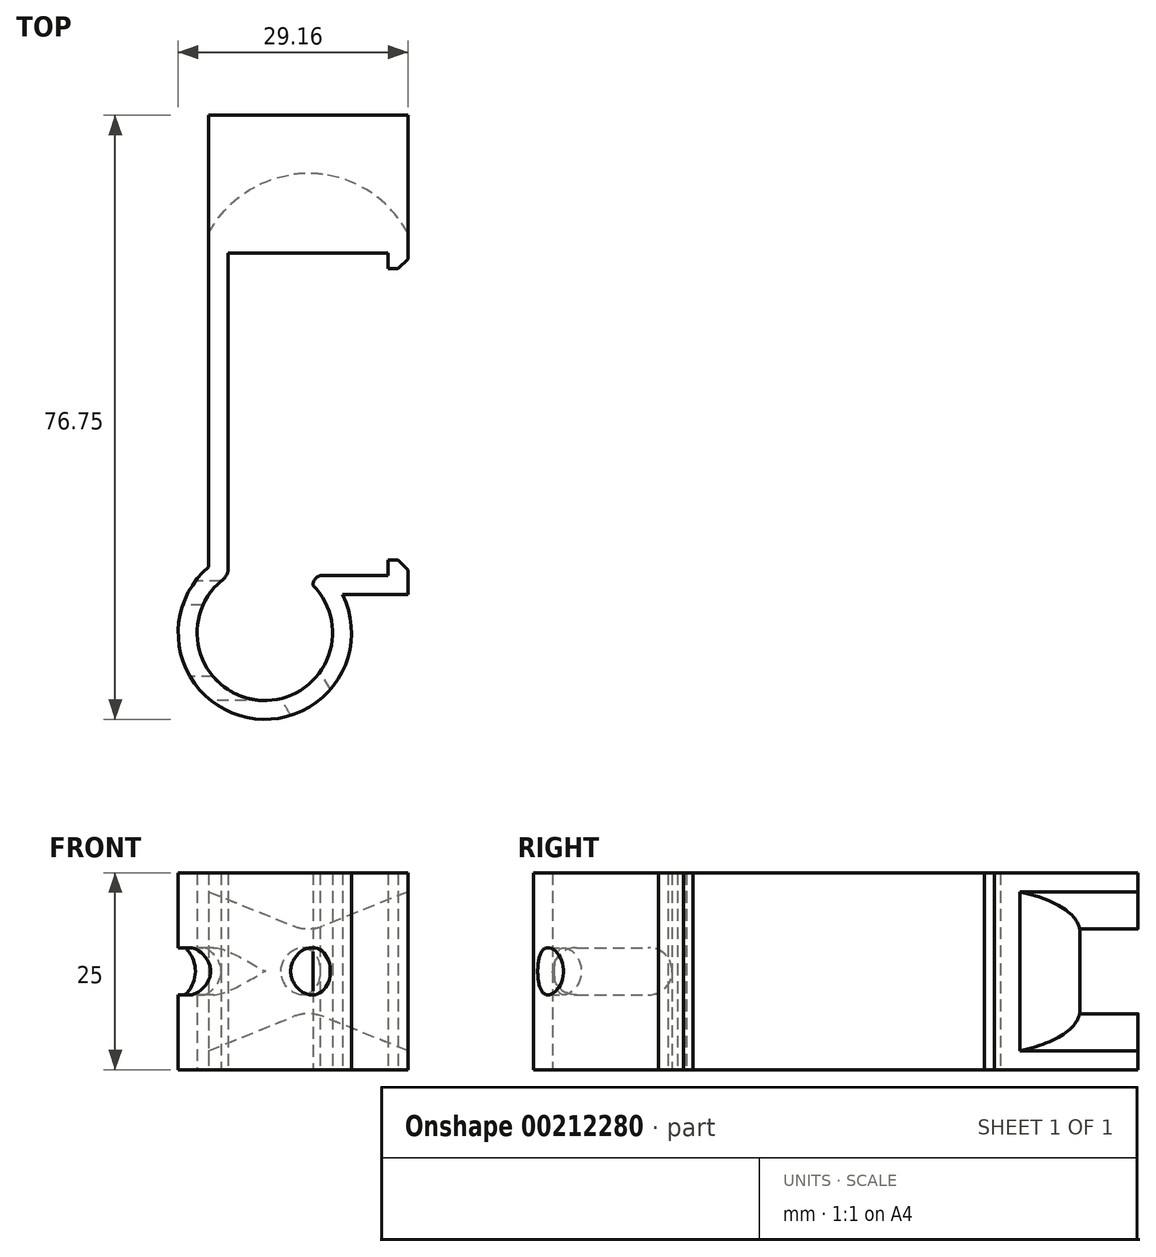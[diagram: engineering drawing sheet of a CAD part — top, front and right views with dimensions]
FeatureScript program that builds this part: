
annotation { "Feature Type Name" : "Feature", "Feature Type Description" : "" }
export const myFeature = defineFeature(function(context is Context, id is Id, definition is map)
    precondition{}
    {
        {
            var Q0;
            Q0=qCreatedBy(makeId("Top.planeOp"),FACE);
            var sketch = newSketch(context, id + "F0", { "sketchPlane" : qUnion([Q0])});
            skLineSegment(sketch, "E0", {"start": v(0, 0) * mm, "end": v(20.3, 0) * mm});
            skLineSegment(sketch, "E1", {"start": v(20.3, 0) * mm, "end": v(20.3, -2) * mm});
            skLineSegment(sketch, "E2", {"start": v(20.3, -2) * mm, "end": v(21.55, -2) * mm});
            skLineSegment(sketch, "E3", {"start": v(22.8, -0.75) * mm, "end": v(22.8, 2.5) * mm});
            skLineSegment(sketch, "E4", {"start": v(22.8, 2.5) * mm, "end": v(-2.5, 2.5) * mm});
            skLineSegment(sketch, "E5", {"start": v(-2.5, 2.5) * mm, "end": v(-2.5, -39.87) * mm});
            skLineSegment(sketch, "E6", {"start": v(0, 0) * mm, "end": v(0, -40.08) * mm});
            skLineSegment(sketch, "E7", {"start": v(21.55, -2) * mm, "end": v(22.8, -0.75) * mm});
            skPoint(sketch, "E8.orphan", {"position": v(22.8, -2) * mm});
            skLineSegment(sketch, "E9", {"start": v(0, -20.5) * mm, "end": v(14.17, -20.5) * mm});
            skPoint(sketch, "E9.endSnap0", {"position": v(0, -20.5) * mm});
            skPoint(sketch, "E10.MirrorP", {"position": v(22.8, -39) * mm});
            skLineSegment(sketch, "E11.MirrorCS", {"start": v(20.3, -41) * mm, "end": v(20.3, -39) * mm});
            skLineSegment(sketch, "E12.MirrorCS", {"start": v(20.3, -39) * mm, "end": v(21.55, -39) * mm});
            skLineSegment(sketch, "E13.MirrorCS", {"start": v(21.55, -39) * mm, "end": v(22.8, -40.25) * mm});
            skLineSegment(sketch, "E14.MirrorCS", {"start": v(22.8, -40.25) * mm, "end": v(22.8, -43.4) * mm});
            skLineSegment(sketch, "E15", {"start": v(20.3, -41) * mm, "end": v(11.67, -41) * mm});
            skLineSegment(sketch, "E16", {"start": v(22.8, -43.4) * mm, "end": v(14.52, -43.4) * mm});
            skPoint(sketch, "E17.orphan", {"position": v(9.28, -43.4) * mm});
            skArc(sketch, "E18", {"start": v(-0.56, -41.4) * mm, "mid": v(4.02, -56.83) * mm, "end": v(10.78, -42.21) * mm});
            skArc(sketch, "E19.0", {"start": v(-2.5, -39.87) * mm, "mid": v(2.4, -59.02) * mm, "end": v(14.52, -43.4) * mm});
            skArc(sketch, "E20", {"start": v(11.67, -41) * mm, "mid": v(11, -41.44) * mm, "end": v(10.78, -42.21) * mm});
            skPoint(sketch, "E21.orphan", {"position": v(9.28, -41) * mm});
            skPoint(sketch, "E22.orphan", {"position": v(-2.5, -41) * mm});
            skArc(sketch, "E23", {"start": v(-0.9, -41.67) * mm, "mid": v(-0.25, -40.99) * mm, "end": v(0, -40.08) * mm});
            skPoint(sketch, "E24.orphan", {"position": v(0, -41) * mm});
            skSolve(sketch);
        }
        {
            var Q0;
            Q0 = qSketchRegion(id + "F0", true);
            extrude(context, id + "F1", {"entities" : qUnion([Q0]), "depth" : 25 * mm});
        }
        {
            var Q0;
            Q0=makeQuery(id+"F1.opExtrude","CAP_FACE",FACE,{"disambiguationData":[OSD([sQuery(id+"F0.wireOp",EDGE,"E0"),sQuery(id+"F0.wireOp",EDGE,"E1"),sQuery(id+"F0.wireOp",EDGE,"E2"),sQuery(id+"F0.wireOp",EDGE,"E3"),sQuery(id+"F0.wireOp",EDGE,"E4"),sQuery(id+"F0.wireOp",EDGE,"E5"),sQuery(id+"F0.wireOp",EDGE,"E6"),sQuery(id+"F0.wireOp",EDGE,"E7"),sQuery(id+"F0.wireOp",EDGE,"E11.MirrorCS"),sQuery(id+"F0.wireOp",EDGE,"E12.MirrorCS"),sQuery(id+"F0.wireOp",EDGE,"E13.MirrorCS"),sQuery(id+"F0.wireOp",EDGE,"E14.MirrorCS"),sQuery(id+"F0.wireOp",EDGE,"E15"),sQuery(id+"F0.wireOp",EDGE,"E16"),sQuery(id+"F0.wireOp",EDGE,"E18"),sQuery(id+"F0.wireOp",EDGE,"E19.0"),sQuery(id+"F0.wireOp",EDGE,"E20"),sQuery(id+"F0.wireOp",EDGE,"E23")])],"isStart":false});
            var sketch = newSketch(context, id + "F2", { "sketchPlane" : qUnion([Q0])});
            skLineSegment(sketch, "E25", {"start": v(4.24, -56.84) * mm, "end": v(-14.11, -38.5) * mm});
            skLineSegment(sketch, "E26", {"start": v(4.24, -56.84) * mm, "end": v(28.92, -42.6) * mm});
            skLineSegment(sketch, "E27", {"start": v(-16.07, -56.84) * mm, "end": v(26.6, -56.84) * mm});
            skSolve(sketch);
        }
        {
            var Q0;
            Q0=sQuery(id+"F2.wireOp",EDGE,"E26");
            cPlane(context, id + "F3", {"entities" : qUnion([Q0]), "cplaneType" : CPlaneType.LINE_ANGLE, "offset" : 25 * mm, "angle" : 0 * degree, "width" : 150 * mm, "height" : 150 * mm});
        }
        {
            var Q0;
            Q0=qCreatedBy(id+"F3.planeOp",FACE);
            var sketch = newSketch(context, id + "F4", { "sketchPlane" : qUnion([Q0])});
            skLineSegment(sketch, "E28.0", {"start": v(11.5, 25) * mm, "end": v(28.71, 25) * mm});
            skLineSegment(sketch, "E28.1", {"start": v(11.5, 0) * mm, "end": v(28.71, 0) * mm});
            skLineSegment(sketch, "E29", {"start": v(11.5, 25) * mm, "end": v(11.5, 0) * mm});
            skLineSegment(sketch, "E30", {"start": v(11.5, 12.5) * mm, "end": v(28.71, 12.5) * mm});
            skCircle(sketch, "E31", {"center": v(19.5, 12.5) * mm, "radius": 3 * mm});
            skSolve(sketch);
        }
        {
            var Q0;
            Q0 = qSketchRegion(id + "F4", true);
            extrude(context, id + "F5", {"entities" : qUnion([Q0]), "operationType" : NewBodyOperationType.REMOVE, "oppositeDirection" : true, "depth" : 7.7 * mm});
        }
        {
            var Q0;
            Q0=makeQuery(id+"F1.opExtrude","SWEPT_FACE",FACE,{"disambiguationData":[OSD([sQuery(id+"F0.wireOp",EDGE,"E5")])]});
            var sketch = newSketch(context, id + "F6", { "sketchPlane" : qUnion([Q0])});
            skLineSegment(sketch, "E32.0", {"start": v(41.67, 0) * mm, "end": v(56.85, 0) * mm});
            skLineSegment(sketch, "E33.0", {"start": v(41.67, 25) * mm, "end": v(56.85, 25) * mm});
            skLineSegment(sketch, "E34", {"start": v(41.67, 0) * mm, "end": v(41.67, 25) * mm});
            skLineSegment(sketch, "E35", {"start": v(44.67, 12.5) * mm, "end": v(53.85, 12.5) * mm});
            skLineSegment(sketch, "E36.bottom", {"start": v(44.7, 15.5) * mm, "end": v(53.8, 15.5) * mm});
            skLineSegment(sketch, "E36.top", {"start": v(44.7, 9.5) * mm, "end": v(53.8, 9.5) * mm});
            skPoint(sketch, "E36.middle", {"position": v(49.26, 12.5) * mm});
            skArc(sketch, "E37", {"start": v(44.7, 15.5) * mm, "mid": v(41.67, 12.5) * mm, "end": v(44.7, 9.5) * mm});
            skArc(sketch, "E38", {"start": v(53.8, 9.5) * mm, "mid": v(56.85, 12.5) * mm, "end": v(53.8, 15.5) * mm});
            skPoint(sketch, "E39.orphan", {"position": v(41.67, 12.5) * mm});
            skPoint(sketch, "E40.orphan", {"position": v(56.85, 12.5) * mm});
            skSolve(sketch);
        }
        {
            var Q0;
            Q0 = qSketchRegion(id + "F6", true);
            extrude(context, id + "F7", {"entities" : qUnion([Q0]), "operationType" : NewBodyOperationType.REMOVE, "oppositeDirection" : true, "depth" : 7.2 * mm, "hasSecondDirection" : true, "secondDirectionOppositeDirection" : false, "secondDirectionDepth" : 25 * mm});
        }
        {
            var Q0;
            Q0=makeQuery(id+"F1.opExtrude","SWEPT_FACE",FACE,{"disambiguationData":[OSD([sQuery(id+"F0.wireOp",EDGE,"E4")])]});
            var sketch = newSketch(context, id + "F8", { "sketchPlane" : qUnion([Q0])});
            skLineSegment(sketch, "E41.0.0", {"start": v(2.5, 25) * mm, "end": v(-22.8, 25) * mm});
            skLineSegment(sketch, "E41.0.2", {"start": v(-22.8, 0) * mm, "end": v(2.5, 0) * mm});
            skLineSegment(sketch, "E42", {"start": v(2.5, 0) * mm, "end": v(2.5, 25) * mm});
            skLineSegment(sketch, "E43", {"start": v(2.5, 12.5) * mm, "end": v(-11.18, 12.5) * mm});
            skLineSegment(sketch, "E44", {"start": v(2.5, 0) * mm, "end": v(2.5, 2.4) * mm});
            skLineSegment(sketch, "E45", {"start": v(2.5, 2.4) * mm, "end": v(-10.15, 7.5) * mm});
            skPoint(sketch, "E45.endSnap0", {"position": v(-10.15, 25) * mm});
            skLineSegment(sketch, "E46", {"start": v(-10.15, 0) * mm, "end": v(-10.15, 3.62) * mm});
            skLineSegment(sketch, "E47.MirrorCS", {"start": v(-22.8, 2.4) * mm, "end": v(-10.15, 7.5) * mm});
            skLineSegment(sketch, "E48.MirrorCS", {"start": v(-22.8, 0) * mm, "end": v(-22.8, 2.4) * mm});
            skLineSegment(sketch, "E49.MirrorCS", {"start": v(2.5, 25) * mm, "end": v(2.5, 22.6) * mm});
            skLineSegment(sketch, "E50.MirrorCS", {"start": v(-22.8, 25) * mm, "end": v(2.5, 25) * mm});
            skLineSegment(sketch, "E51.MirrorCS", {"start": v(2.5, 22.6) * mm, "end": v(-10.15, 17.5) * mm});
            skLineSegment(sketch, "E52.MirrorCS", {"start": v(-10.15, 25) * mm, "end": v(-10.15, 21.38) * mm});
            skLineSegment(sketch, "E53.MirrorCS", {"start": v(-22.8, 25) * mm, "end": v(-22.8, 22.6) * mm});
            skLineSegment(sketch, "E54.MirrorCS", {"start": v(-22.8, 22.6) * mm, "end": v(-10.15, 17.5) * mm});
            skSolve(sketch);
        }
        {
            var Q0;
            Q0=makeQuery(id+"F2.imprint","IMPRINT",FACE,{"disambiguationData":[TD([[makeQuery(id+"F2.imprint","IMPRINT",EDGE,{"derivedFrom":makeQuery(id+"F1.opExtrude","CAP_EDGE",EDGE,{"disambiguationData":[OSD([sQuery(id+"F0.wireOp",EDGE,"E0")])],"isStart":false})}),1.0]])]});
            var sketch = newSketch(context, id + "F9", { "sketchPlane" : qUnion([Q0])});
            skLineSegment(sketch, "E55.0", {"start": v(22.8, 2.5) * mm, "end": v(-2.5, 2.5) * mm});
            skArc(sketch, "E56", {"start": v(22.8, 2.5) * mm, "mid": v(10.15, 10.1) * mm, "end": v(-2.5, 2.5) * mm});
            skArc(sketch, "E57.0", {"start": v(20, 2.5) * mm, "mid": v(10.15, 7.7) * mm, "end": v(0.3, 2.5) * mm});
            skSolve(sketch);
        }
        {
            var Q0;
            Q0 = qSketchRegion(id + "F9", true);
            extrude(context, id + "F10", {"entities" : qUnion([Q0]), "operationType" : NewBodyOperationType.ADD, "oppositeDirection" : true, "depth" : 25 * mm});
        }
        {
            var Q0;
            Q0 = qSketchRegion(id + "F8", true);
            extrude(context, id + "F11", {"entities" : qUnion([Q0]), "operationType" : NewBodyOperationType.ADD, "depth" : 15 * mm});
        }
        {
            var Q0;
            Q0=makeQuery(id+"F11.opExtrude","SWEPT_EDGE",EDGE,{"disambiguationData":[OSD([sQuery(id+"F8.wireOp",EDGE,"E45"),sQuery(id+"F8.wireOp",EDGE,"E47.MirrorCS")])]});
            var Q1;
            Q1=makeQuery(id+"F11.opExtrude","SWEPT_EDGE",EDGE,{"disambiguationData":[OSD([sQuery(id+"F8.wireOp",EDGE,"E51.MirrorCS"),sQuery(id+"F8.wireOp",EDGE,"E54.MirrorCS")])]});
            fillet(context, id + "F12", {"entities" : qUnion([Q0, Q1]), "radius" : 5 * mm, "tangentPropagation" : true, "allowEdgeOverflow" : false});
        }
    });
